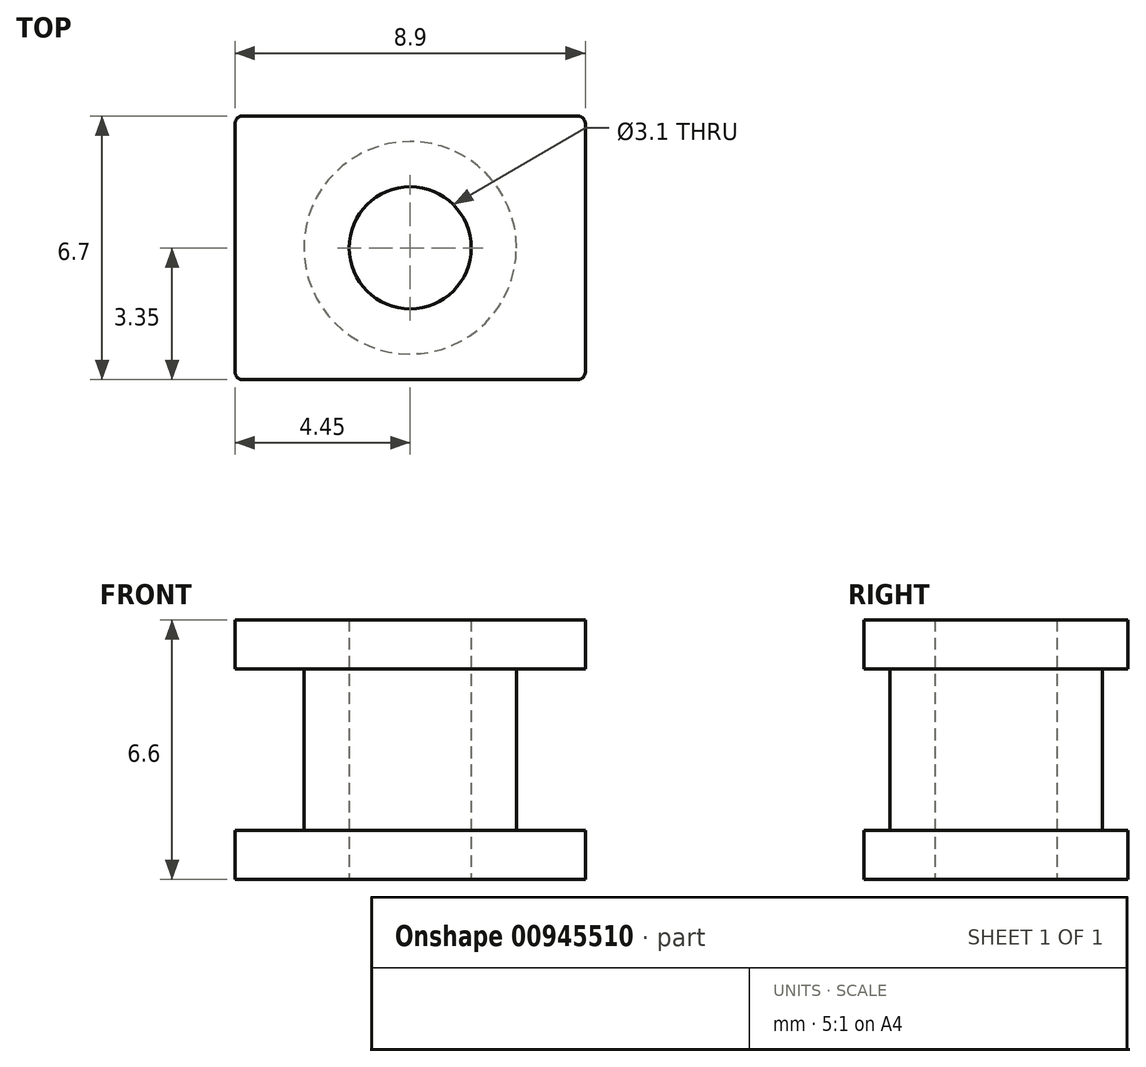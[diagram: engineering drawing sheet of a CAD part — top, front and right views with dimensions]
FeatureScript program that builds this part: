
annotation { "Feature Type Name" : "Feature", "Feature Type Description" : "" }
export const myFeature = defineFeature(function(context is Context, id is Id, definition is map)
    precondition{}
    {
        {
            var Q0;
            Q0=qCreatedBy(makeId("Top.planeOp"),FACE);
            var sketch = newSketch(context, id + "F0", { "sketchPlane" : qUnion([Q0])});
            skCircle(sketch, "E0", {"center": v(0, 0) * mm, "radius": 2.7 * mm});
            skCircle(sketch, "E1", {"center": v(0, 0) * mm, "radius": 1.55 * mm});
            skSolve(sketch);
        }
        {
            var Q0;
            Q0=makeQuery(id+"F0.imprint","IMPRINT",FACE,{"disambiguationData":[TD([[makeQuery(id+"F0.imprint","IMPRINT",EDGE,{"derivedFrom":sQuery(id+"F0.wireOp",EDGE,"E0")}),1.0]])]});
            extrude(context, id + "F1", {"entities" : qUnion([Q0]), "depth" : 4.1 / 2 * mm, "offsetDistance" : 25 * mm});
        }
        {
            var Q0;
            Q0=makeQuery(id+"F1.opExtrude","CAP_FACE",FACE,{"disambiguationData":[OSD([sQuery(id+"F0.wireOp",EDGE,"E0"),sQuery(id+"F0.wireOp",EDGE,"E1")])],"isStart":false});
            var sketch = newSketch(context, id + "F2", { "sketchPlane" : qUnion([Q0])});
            skLineSegment(sketch, "E2.bottom", {"start": v(4.45, -3.35) * mm, "end": v(-4.45, -3.35) * mm});
            skLineSegment(sketch, "E2.top", {"start": v(4.45, 3.35) * mm, "end": v(-4.45, 3.35) * mm});
            skLineSegment(sketch, "E2.left", {"start": v(4.45, -3.35) * mm, "end": v(4.45, 3.35) * mm});
            skLineSegment(sketch, "E2.right", {"start": v(-4.45, -3.35) * mm, "end": v(-4.45, 3.35) * mm});
            skPoint(sketch, "E2.middle", {"position": v(0, 0) * mm});
            skCircle(sketch, "E3", {"center": v(0, 0) * mm, "radius": 1.55 * mm});
            skSolve(sketch);
        }
        {
            var Q0;
            Q0=makeQuery(id+"F2.imprint","IMPRINT",FACE,{"disambiguationData":[TD([[makeQuery(id+"F2.imprint","IMPRINT",EDGE,{"derivedFrom":sQuery(id+"F2.wireOp",EDGE,"E2.bottom")}),-1.0]])]});
            var Q1;
            Q1=makeQuery(id+"F2.imprint","IMPRINT",FACE,{"disambiguationData":[TD([[makeQuery(id+"F2.imprint","IMPRINT",EDGE,{"derivedFrom":sQuery(id+"F2.wireOp",EDGE,"E3")}),-1.0]])]});
            extrude(context, id + "F3", {"entities" : qUnion([Q0, Q1]), "operationType" : NewBodyOperationType.ADD, "depth" : ((6.6 - 4.1) / 2) * mm, "offsetDistance" : 25 * mm});
        }
        {
            var Q0;
            Q0=makeQuery(id+"F3.opExtrude","SWEPT_EDGE",EDGE,{"disambiguationData":[OSD([sQuery(id+"F2.wireOp",EDGE,"E2.bottom"),sQuery(id+"F2.wireOp",EDGE,"E2.left")])]});
            var Q1;
            Q1=makeQuery(id+"F3.opExtrude","SWEPT_EDGE",EDGE,{"disambiguationData":[OSD([sQuery(id+"F2.wireOp",EDGE,"E2.bottom"),sQuery(id+"F2.wireOp",EDGE,"E2.right")])]});
            var Q2;
            Q2=makeQuery(id+"F3.opExtrude","SWEPT_EDGE",EDGE,{"disambiguationData":[OSD([sQuery(id+"F2.wireOp",EDGE,"E2.top"),sQuery(id+"F2.wireOp",EDGE,"E2.right")])]});
            var Q3;
            Q3=makeQuery(id+"F3.opExtrude","SWEPT_EDGE",EDGE,{"disambiguationData":[OSD([sQuery(id+"F2.wireOp",EDGE,"E2.top"),sQuery(id+"F2.wireOp",EDGE,"E2.left")])]});
            fillet(context, id + "F4", {"entities" : qUnion([Q0, Q1, Q2, Q3]), "radius" : 0.2 * mm, "tangentPropagation" : true, "allowEdgeOverflow" : false});
        }
        {
            var Q0;
            Q0=makeQuery(id+"F1.opExtrude","SWEPT_BODY",BODY,{"disambiguationData":[OSD([sQuery(id+"F0.wireOp",EDGE,"E0"),sQuery(id+"F0.wireOp",EDGE,"E1")])]});
            var Q1;
            Q1=qCreatedBy(makeId("Top.planeOp"),FACE);
            mirror(context, id + "F5", {"operationType" : NewBodyOperationType.ADD, "entities" : qUnion([Q0]), "mirrorPlane" : qUnion([Q1])});
        }
    });
